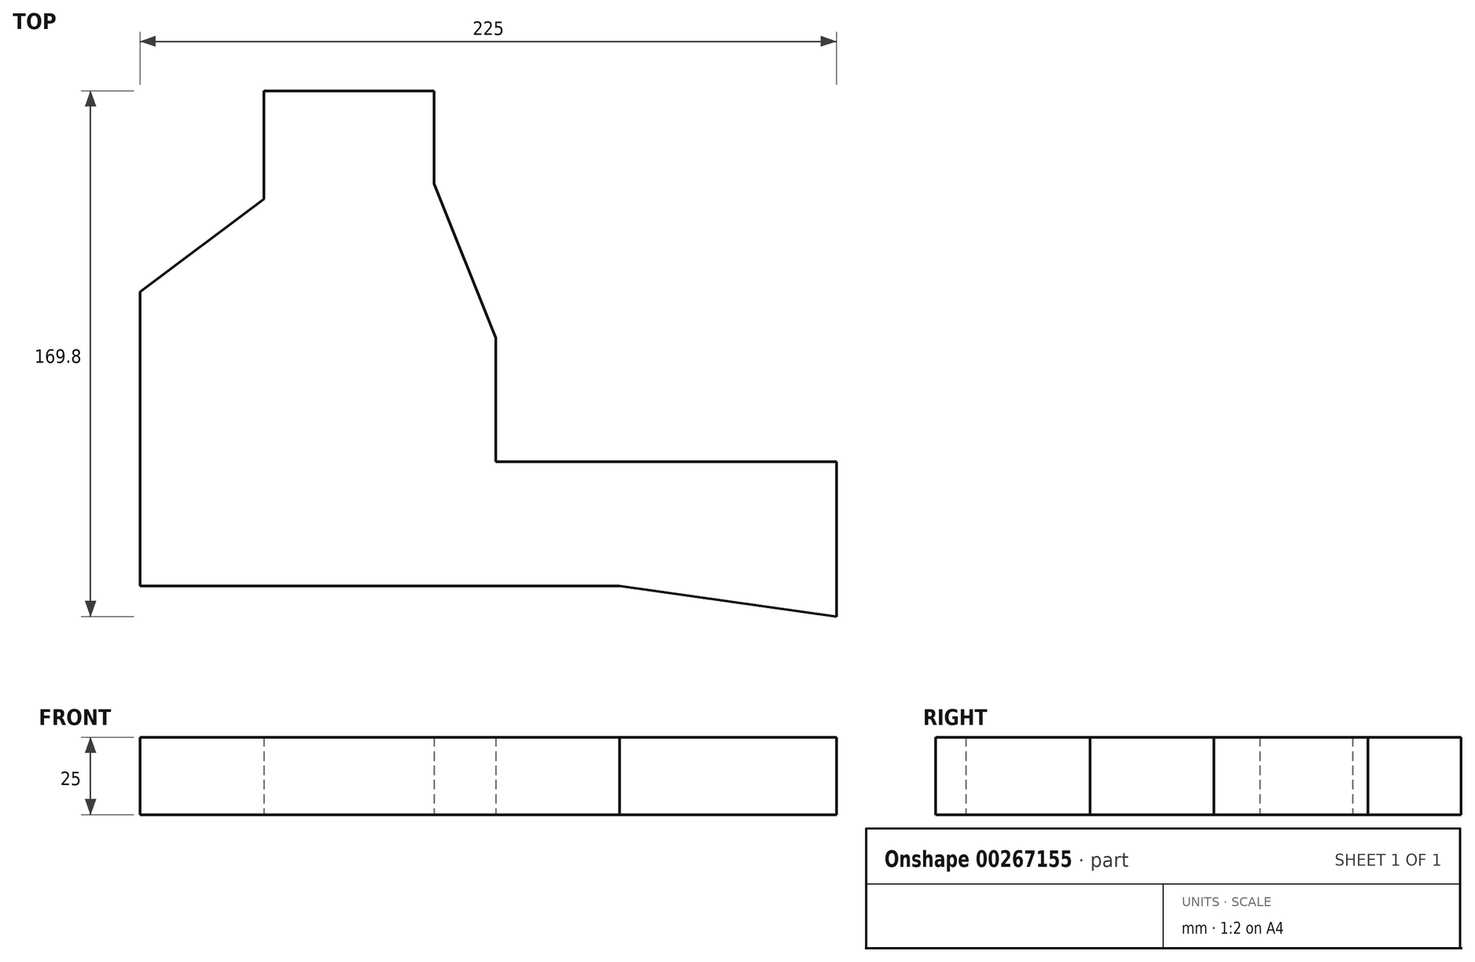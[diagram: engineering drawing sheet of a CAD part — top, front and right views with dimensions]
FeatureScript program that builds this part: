
annotation { "Feature Type Name" : "Feature", "Feature Type Description" : "" }
export const myFeature = defineFeature(function(context is Context, id is Id, definition is map)
    precondition{}
    {
        {
            var Q0;
            Q0=qCreatedBy(makeId("Top.planeOp"),FACE);
            var sketch = newSketch(context, id + "F0", { "sketchPlane" : qUnion([Q0])});
            skLineSegment(sketch, "E0", {"start": v(-124.03, -33.23) * mm, "end": v(30.97, -33.23) * mm});
            skLineSegment(sketch, "E1", {"start": v(-124.03, -33.23) * mm, "end": v(-124.03, 61.77) * mm});
            skLineSegment(sketch, "E2", {"start": v(-84.03, 91.77) * mm, "end": v(-124.03, 61.77) * mm});
            skLineSegment(sketch, "E3", {"start": v(-84.03, 91.77) * mm, "end": v(-84.03, 126.77) * mm});
            skLineSegment(sketch, "E4", {"start": v(-84.03, 126.77) * mm, "end": v(-29.03, 126.77) * mm});
            skLineSegment(sketch, "E5", {"start": v(-29.03, 126.77) * mm, "end": v(-29.03, 96.77) * mm});
            skLineSegment(sketch, "E6", {"start": v(-29.03, 96.77) * mm, "end": v(-9.03, 46.97) * mm});
            skLineSegment(sketch, "E7", {"start": v(-9.03, 46.97) * mm, "end": v(-9.03, 6.97) * mm});
            skLineSegment(sketch, "E8", {"start": v(100.97, 6.97) * mm, "end": v(100.97, -43.03) * mm});
            skLineSegment(sketch, "E9", {"start": v(-9.03, 6.97) * mm, "end": v(100.97, 6.97) * mm});
            skLineSegment(sketch, "E10", {"start": v(30.97, -33.23) * mm, "end": v(100.97, -43.03) * mm});
            skSolve(sketch);
        }
        {
            var Q0;
            Q0 = qSketchRegion(id + "F0", true);
            extrude(context, id + "F1", {"entities" : qUnion([Q0]), "depth" : 25 * mm});
        }
    });
